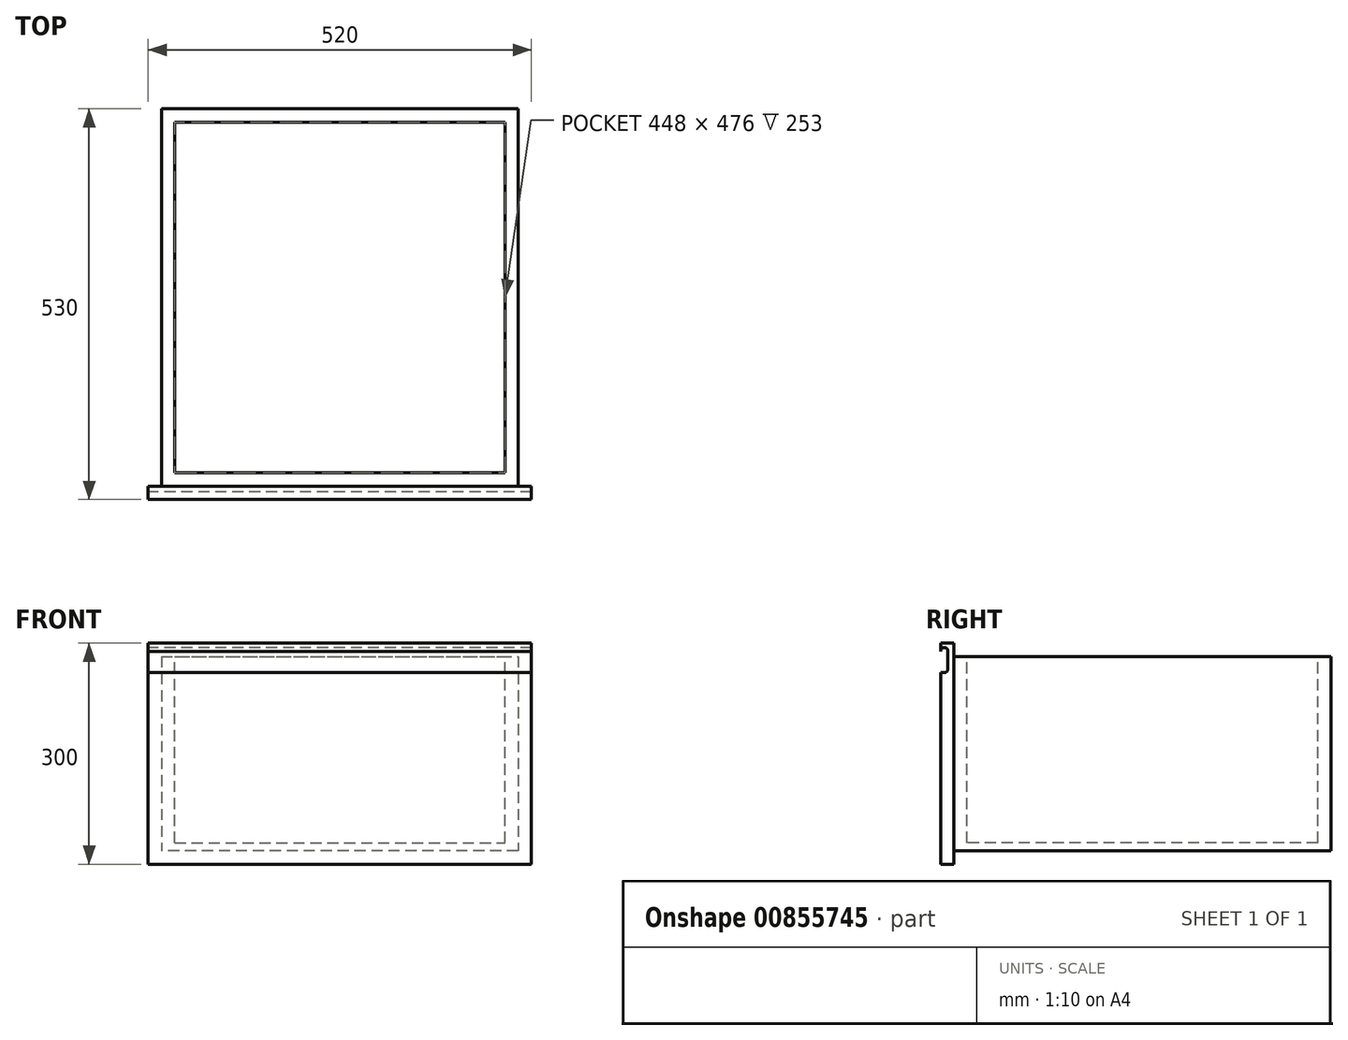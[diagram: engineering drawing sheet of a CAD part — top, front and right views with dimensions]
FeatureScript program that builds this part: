
annotation { "Feature Type Name" : "Feature", "Feature Type Description" : "" }
export const myFeature = defineFeature(function(context is Context, id is Id, definition is map)
    precondition{}
    {
        {
            var Q0;
            Q0=qCreatedBy(makeId("Front.planeOp"),FACE);
            var sketch = newSketch(context, id + "F0", { "sketchPlane" : qUnion([Q0])});
            skLineSegment(sketch, "E0", {"start": v(0, 300) * mm, "end": v(520, 300) * mm});
            skLineSegment(sketch, "E1", {"start": v(520, 0) * mm, "end": v(0, 0) * mm});
            skLineSegment(sketch, "E2", {"start": v(520, 300) * mm, "end": v(520, 0) * mm});
            skLineSegment(sketch, "E3", {"start": v(0, 300) * mm, "end": v(0, 0) * mm});
            skLineSegment(sketch, "E4.0", {"start": v(18, 282) * mm, "end": v(502, 282) * mm});
            skLineSegment(sketch, "E4.1", {"start": v(18, 282) * mm, "end": v(18, 18) * mm});
            skLineSegment(sketch, "E4.2", {"start": v(502, 18) * mm, "end": v(18, 18) * mm});
            skLineSegment(sketch, "E4.3", {"start": v(502, 282) * mm, "end": v(502, 18) * mm});
            skSolve(sketch);
        }
        {
            var Q0;
            Q0 = qSketchRegion(id + "F0", true);
            extrude(context, id + "F1", {"entities" : qUnion([Q0]), "oppositeDirection" : true, "depth" : 18 * mm, "offsetDistance" : 25 * mm});
        }
        {
            var Q0;
            Q0=makeQuery(id+"F0.imprint","IMPRINT",FACE,{"disambiguationData":[TD([[makeQuery(id+"F0.imprint","IMPRINT",EDGE,{"derivedFrom":sQuery(id+"F0.wireOp",EDGE,"E4.0")}),-1.0]])]});
            extrude(context, id + "F2", {"entities" : qUnion([Q0]), "operationType" : NewBodyOperationType.ADD, "oppositeDirection" : true, "depth" : 530 * mm, "offsetDistance" : 25 * mm});
        }
        {
            var Q0;
            Q0=makeQuery(id+"F2.opExtrude","SWEPT_FACE",FACE,{"disambiguationData":[OSD([sQuery(id+"F0.wireOp",EDGE,"E4.0")])]});
            var sketch = newSketch(context, id + "F3", { "sketchPlane" : qUnion([Q0])});
            skLineSegment(sketch, "E5.bottom", {"start": v(18, 530) * mm, "end": v(502, 530) * mm});
            skLineSegment(sketch, "E5.top", {"start": v(18, 18) * mm, "end": v(502, 18) * mm});
            skLineSegment(sketch, "E5.left", {"start": v(18, 530) * mm, "end": v(18, 18) * mm});
            skLineSegment(sketch, "E5.right", {"start": v(502, 530) * mm, "end": v(502, 18) * mm});
            skLineSegment(sketch, "E6.0", {"start": v(36, 512) * mm, "end": v(484, 512) * mm});
            skLineSegment(sketch, "E6.1", {"start": v(36, 512) * mm, "end": v(36, 36) * mm});
            skLineSegment(sketch, "E6.2", {"start": v(36, 36) * mm, "end": v(484, 36) * mm});
            skLineSegment(sketch, "E6.3", {"start": v(484, 512) * mm, "end": v(484, 36) * mm});
            skSolve(sketch);
        }
        {
            var Q0;
            Q0=makeQuery(id+"F3.imprint","IMPRINT",FACE,{"disambiguationData":[TD([[makeQuery(id+"F3.imprint","IMPRINT",EDGE,{"derivedFrom":sQuery(id+"F3.wireOp",EDGE,"E6.0")}),-1.0]])]});
            extrude(context, id + "F4", {"entities" : qUnion([Q0]), "operationType" : NewBodyOperationType.REMOVE, "oppositeDirection" : true, "depth" : 253 * mm, "offsetDistance" : 25 * mm});
        }
        {
            var Q0;
            Q0=makeQuery(id+"F1.opExtrude","SWEPT_FACE",FACE,{"disambiguationData":[OSD([sQuery(id+"F0.wireOp",EDGE,"E3")])]});
            var sketch = newSketch(context, id + "F5", { "sketchPlane" : qUnion([Q0])});
            skLineSegment(sketch, "E7", {"start": v(0, 260) * mm, "end": v(-5, 260) * mm});
            skLineSegment(sketch, "E8", {"start": v(-10, 265) * mm, "end": v(-10, 289) * mm});
            skArc(sketch, "E9", {"start": v(0, 289) * mm, "mid": v(-5, 294) * mm, "end": v(-10, 289) * mm});
            skPoint(sketch, "E10.visualSharp", {"position": v(-10, 260) * mm});
            skArc(sketch, "E10.filletArc", {"start": v(-10, 265) * mm, "mid": v(-8.54, 261.46) * mm, "end": v(-5, 260) * mm});
            skSolve(sketch);
        }
        {
            var Q0;
            {var subQ1=sQuery(id+"F5.wireOp",EDGE,"E7");Q0=makeQuery(id+"F5.imprint","IMPRINT",FACE,{"disambiguationData":[TD([[makeQuery(id+"F5.imprint","IMPRINT",EDGE,{"derivedFrom":subQ1}),-1.0]])]});}
            extrude(context, id + "F6", {"entities" : qUnion([Q0]), "operationType" : NewBodyOperationType.REMOVE, "oppositeDirection" : true, "depth" : 545 * mm, "offsetDistance" : 25 * mm});
        }
    });
